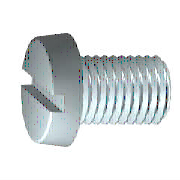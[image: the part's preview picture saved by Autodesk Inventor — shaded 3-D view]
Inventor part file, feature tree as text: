
AUTODESK INVENTOR PART (.ipt)
format: ipt  version: 2015 (Build 190159000, 159)  size: 190,976 bytes
history: native  units: mm (DEFAULTED — no unit token found)
features: sketch x2, other x1, extrude x1, plane x1
ambient origin geometry x7: Origin, YZ Plane, XZ Plane, X Axis, Y Axis, Z Axis, Center Point
bodies: Body1 (feature_tree)
feature tree (5):
  other  "Bryła"
  sketch  "Szkic2"
  extrude  "Szczelina"  Depth=12.0mm
  plane  "Work Plane1"
  sketch  "Szkic1"
